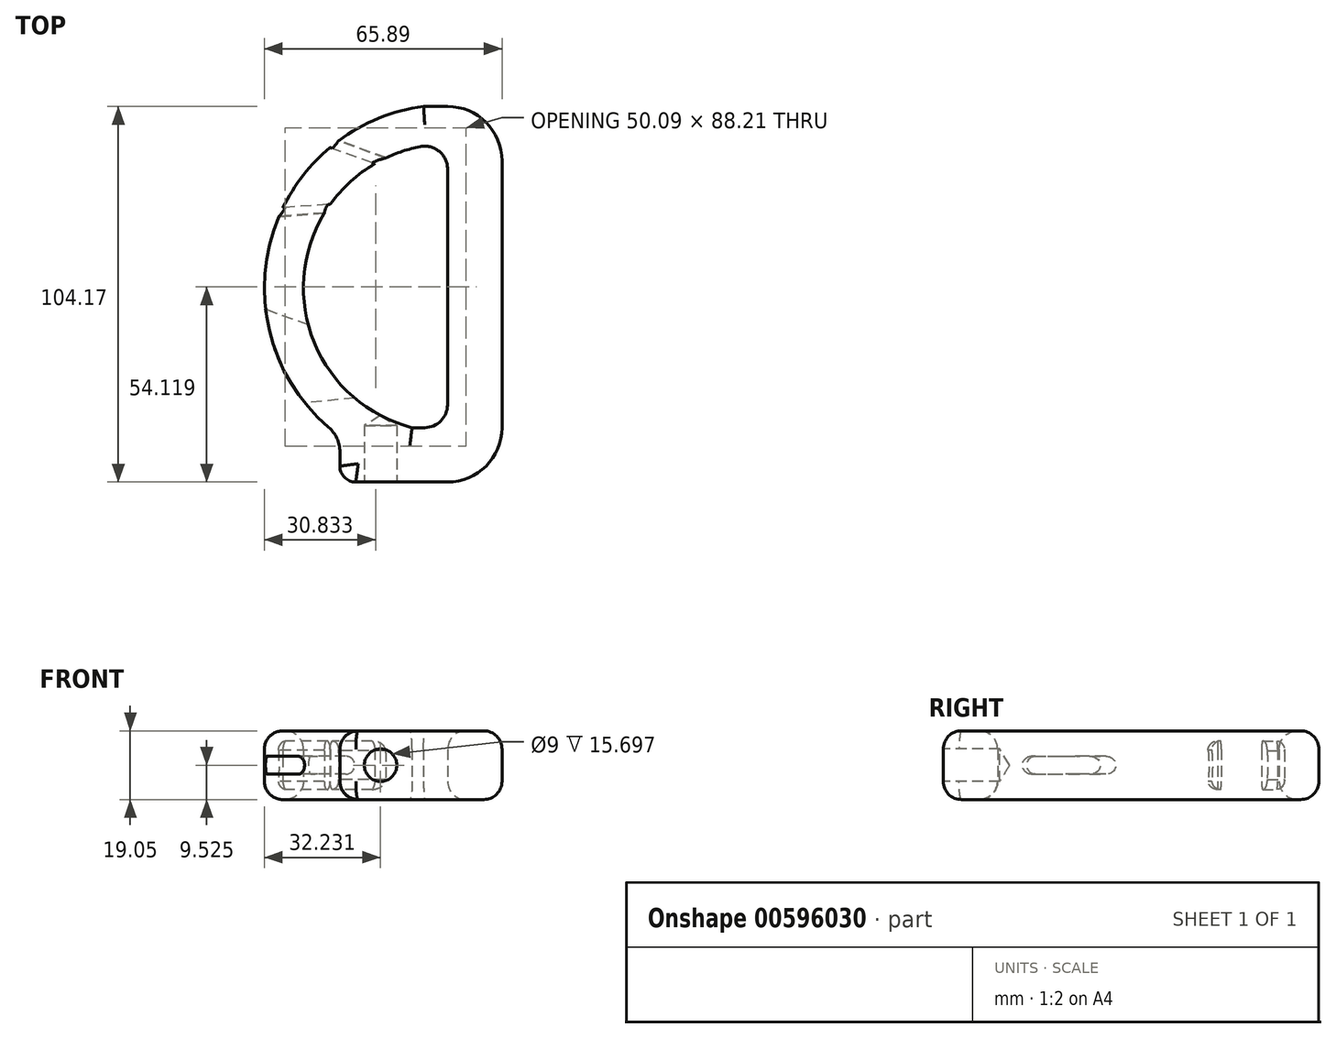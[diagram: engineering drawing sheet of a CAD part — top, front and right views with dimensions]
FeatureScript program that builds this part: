
annotation { "Feature Type Name" : "Feature", "Feature Type Description" : "" }
export const myFeature = defineFeature(function(context is Context, id is Id, definition is map)
    precondition{}
    {
        {
            var Q0;
            Q0=qCreatedBy(makeId("Top.planeOp"),FACE);
            var sketch = newSketch(context, id + "F0", { "sketchPlane" : qUnion([Q0])});
            skArc(sketch, "E0", {"start": v(-6.66, 50.36) * mm, "mid": v(-48.71, 14.41) * mm, "end": v(-33, -38.63) * mm});
            skArc(sketch, "E1", {"start": v(-7.55, 39.23) * mm, "mid": v(-39.93, 1.17) * mm, "end": v(-9.83, -38.72) * mm});
            skLineSegment(sketch, "E2", {"start": v(0, 50.36) * mm, "end": v(-6.66, 50.36) * mm});
            skLineSegment(sketch, "E3", {"start": v(15.1, 35.27) * mm, "end": v(15.1, -38.72) * mm});
            skLineSegment(sketch, "E4", {"start": v(-29.85, -49.4) * mm, "end": v(-29.85, -45.45) * mm});
            skLineSegment(sketch, "E5", {"start": v(0, 33) * mm, "end": v(0, -32.37) * mm});
            skLineSegment(sketch, "E6", {"start": v(-6.35, -38.72) * mm, "end": v(-9.83, -38.72) * mm});
            skPoint(sketch, "E7", {"position": v(-50.8, 0) * mm});
            skPoint(sketch, "E8", {"position": v(-44.25, -24.96) * mm});
            skPoint(sketch, "E9", {"position": v(-47.9, 16.9) * mm});
            skLineSegment(sketch, "E10", {"start": v(-25.43, -53.8) * mm, "end": v(0, -53.8) * mm});
            skPoint(sketch, "E11.visualSharp", {"position": v(15.1, -53.8) * mm});
            skArc(sketch, "E11.filletArc", {"start": v(0, -53.8) * mm, "mid": v(10.67, -49.39) * mm, "end": v(15.1, -38.72) * mm});
            skPoint(sketch, "E12.visualSharp", {"position": v(15.1, 50.36) * mm});
            skArc(sketch, "E12.filletArc", {"start": v(15.1, 35.27) * mm, "mid": v(10.67, 45.94) * mm, "end": v(0, 50.36) * mm});
            skPoint(sketch, "E13.visualSharp", {"position": v(-29.85, -41.1) * mm});
            skArc(sketch, "E13.filletArc", {"start": v(-29.85, -45.45) * mm, "mid": v(-30.67, -41.7) * mm, "end": v(-33, -38.63) * mm});
            skPoint(sketch, "E14.visualSharp", {"position": v(-29.85, -53.8) * mm});
            skArc(sketch, "E14.filletArc", {"start": v(-29.85, -49.4) * mm, "mid": v(-28.55, -52.51) * mm, "end": v(-25.43, -53.8) * mm});
            skPoint(sketch, "E15.visualSharp", {"position": v(0, 39.95) * mm});
            skArc(sketch, "E15.filletArc", {"start": v(0, 33) * mm, "mid": v(-2.3, 37.89) * mm, "end": v(-7.55, 39.23) * mm});
            skArc(sketch, "E16.filletArc", {"start": v(-6.35, -38.72) * mm, "mid": v(-1.86, -36.86) * mm, "end": v(0, -32.37) * mm});
            skPoint(sketch, "E17", {"position": v(-50.65, -3.9) * mm});
            skPoint(sketch, "E18", {"position": v(-36.28, 35.56) * mm});
            skSolve(sketch);
        }
        {
            var Q0;
            Q0=makeQuery(id+"F0.imprint","IMPRINT",FACE,{"disambiguationData":[TD([[makeQuery(id+"F0.imprint","IMPRINT",EDGE,{"derivedFrom":sQuery(id+"F0.wireOp",EDGE,"E0")}),1.0]])]});
            extrude(context, id + "F1", {"entities" : qUnion([Q0]), "depth" : 19.05 * mm, "offsetDistance" : 25.4 * mm});
        }
        {
            var Q0;
            Q0=makeQuery(id+"F1.opExtrude","SWEPT_FACE",FACE,{"disambiguationData":[OSD([sQuery(id+"F0.wireOp",EDGE,"E5")])]});
            cPlane(context, id + "F2", {"entities" : qUnion([Q0]), "cplaneType" : CPlaneType.OFFSET, "offset" : 50.8 * mm, "width" : 152.4 * mm, "height" : 152.4 * mm});
        }
        {
            var Q0;
            Q0=makeQuery(id+"F1.opExtrude","SWEPT_FACE",FACE,{"disambiguationData":[OSD([sQuery(id+"F0.wireOp",EDGE,"E10")])]});
            var sketch = newSketch(context, id + "F3", { "sketchPlane" : qUnion([Q0])});
            skPoint(sketch, "E19", {"position": v(-18.57, 9.53) * mm});
            skSolve(sketch);
        }
        {
            var Q0;
            Q0=sQuery(id+"F3.wireOp",VERTEX,"E19");
            var Q1;
            Q1=makeQuery(id+"F1.opExtrude","SWEPT_BODY",BODY,{"disambiguationData":[OSD([sQuery(id+"F0.wireOp",EDGE,"E0"),sQuery(id+"F0.wireOp",EDGE,"E1"),sQuery(id+"F0.wireOp",EDGE,"E2"),sQuery(id+"F0.wireOp",EDGE,"E3"),sQuery(id+"F0.wireOp",EDGE,"E4"),sQuery(id+"F0.wireOp",EDGE,"E5"),sQuery(id+"F0.wireOp",EDGE,"E6"),sQuery(id+"F0.wireOp",EDGE,"E10")])]});
            hole(context, id + "F4", {"style" : HoleStyle.SIMPLE, "endStyle" : HoleEndStyle.BLIND, "standardTappedOrClearance" : lookupTablePath({ "standard" : "ISO", "engagement" : "75%", "pitch" : "1 mm", "size" : "M10", "type" : "Tapped" }), "standardBlindInLast" : lookupTablePath({ "standard" : "ISO", "engagement" : "75%", "pitch" : "1 mm", "size" : "M10", "type" : "Tapped" }), "holeDiameter" : 9 * mm, "showTappedDepth" : true, "holeDepth" : 15.7 * mm, "isTappedThrough" : true, "tappedDepth" : 12.7 * mm, "tapClearance" : 3, "locations" : qUnion([Q0]), "scope" : qUnion([Q1]), "majorDiameter" : 10 * mm});
        }
        {
            var Q0;
            Q0=qCreatedBy(id+"F2.planeOp",FACE);
            var sketch = newSketch(context, id + "F5", { "sketchPlane" : qUnion([Q0])});
            skPoint(sketch, "E20", {"position": v(-17.21, 0) * mm});
            skPoint(sketch, "E21", {"position": v(-35.87, 0) * mm});
            skPoint(sketch, "E22", {"position": v(3.6, 0) * mm});
            skPoint(sketch, "E23", {"position": v(24.65, 0) * mm});
            skLineSegment(sketch, "E24", {"start": v(-35.87, 0) * mm, "end": v(-35.87, 19.05) * mm});
            skLineSegment(sketch, "E25", {"start": v(-17.21, 0) * mm, "end": v(-17.21, 19.05) * mm});
            skLineSegment(sketch, "E26", {"start": v(3.6, 0) * mm, "end": v(3.6, 7.02) * mm});
            skLineSegment(sketch, "E27", {"start": v(24.65, 0) * mm, "end": v(24.65, 7.02) * mm});
            skArc(sketch, "E28", {"start": v(-35.87, 16.26) * mm, "mid": v(-37.56, 15.6) * mm, "end": v(-38.36, 13.97) * mm});
            skArc(sketch, "E29.MirrorCS", {"start": v(-35.87, 2.8) * mm, "mid": v(-37.56, 3.45) * mm, "end": v(-38.36, 5.08) * mm});
            skArc(sketch, "E30", {"start": v(-38.36, 13.97) * mm, "mid": v(-38.54, 9.52) * mm, "end": v(-38.36, 5.08) * mm});
            skLineSegment(sketch, "E31", {"start": v(-35.87, 5.3) * mm, "end": v(-35.87, 13.76) * mm});
            skPoint(sketch, "E32", {"position": v(-35.87, 9.52) * mm});
            skLineSegment(sketch, "E33", {"start": v(-1.84, -3.07) * mm, "end": v(-1.84, 15.98) * mm});
            skArc(sketch, "E34", {"start": v(-14.72, 13.55) * mm, "mid": v(-15.37, 15.45) * mm, "end": v(-17.21, 16.26) * mm});
            skArc(sketch, "E35.MirrorCS", {"start": v(-14.72, 5.5) * mm, "mid": v(-15.37, 3.6) * mm, "end": v(-17.21, 2.8) * mm});
            skArc(sketch, "E36", {"start": v(-14.72, 13.55) * mm, "mid": v(-14.89, 9.52) * mm, "end": v(-14.72, 5.5) * mm});
            skLineSegment(sketch, "E37", {"start": v(-17.21, 5.3) * mm, "end": v(-17.21, 13.76) * mm});
            skPoint(sketch, "E38", {"position": v(-17.21, 9.53) * mm});
            skLineSegment(sketch, "E39", {"start": v(-35.87, 2.8) * mm, "end": v(-17.21, 2.8) * mm});
            skLineSegment(sketch, "E40", {"start": v(-35.87, 16.26) * mm, "end": v(-17.21, 16.26) * mm});
            skArc(sketch, "E41", {"start": v(3.6, 12.03) * mm, "mid": v(1.1, 9.52) * mm, "end": v(3.6, 7.02) * mm});
            skArc(sketch, "E42", {"start": v(24.65, 7.02) * mm, "mid": v(27.15, 9.52) * mm, "end": v(24.65, 12.03) * mm});
            skLineSegment(sketch, "E43", {"start": v(3.6, 12.03) * mm, "end": v(24.65, 12.03) * mm});
            skLineSegment(sketch, "E44", {"start": v(3.6, 7.02) * mm, "end": v(24.65, 7.02) * mm});
            skLineSegment(sketch, "E45.trimOffspring", {"start": v(3.6, 12.03) * mm, "end": v(3.6, 19.05) * mm});
            skLineSegment(sketch, "E46.trimOffspring", {"start": v(24.65, 12.03) * mm, "end": v(24.65, 19.05) * mm});
            skSolve(sketch);
        }
        {
            var Q0;
            Q0=sQuery(id+"F5.wireOp",EDGE,"E33");
            cPlane(context, id + "F6", {"entities" : qUnion([Q0]), "cplaneType" : CPlaneType.LINE_ANGLE, "offset" : 25.4 * mm, "angle" : 20 * degree, "oppositeDirection" : true, "width" : 152.4 * mm, "height" : 152.4 * mm});
        }
        {
            var Q0;
            Q0=qCreatedBy(id+"F6.planeOp",FACE);
            cPlane(context, id + "F7", {"entities" : qUnion([Q0]), "cplaneType" : CPlaneType.OFFSET, "offset" : 12.7 * mm, "oppositeDirection" : true, "width" : 152.4 * mm, "height" : 152.4 * mm});
        }
        {
            var Q0;
            Q0=qCreatedBy(id+"F7.planeOp",FACE);
            var sketch = newSketch(context, id + "F8", { "sketchPlane" : qUnion([Q0])});
            skPoint(sketch, "E47", {"position": v(25.47, 0) * mm});
            skLineSegment(sketch, "E48", {"start": v(13.01, 2.8) * mm, "end": v(13.01, 16.26) * mm});
            skLineSegment(sketch, "E49", {"start": v(25.47, 0) * mm, "end": v(25.47, 19.05) * mm});
            skLineSegment(sketch, "E50", {"start": v(13.01, 5.3) * mm, "end": v(13.01, 13.76) * mm});
            skPoint(sketch, "E51", {"position": v(13.01, 9.53) * mm});
            skArc(sketch, "E52", {"start": v(27.97, 13.55) * mm, "mid": v(27.31, 15.45) * mm, "end": v(25.47, 16.26) * mm});
            skArc(sketch, "E53.MirrorCS", {"start": v(27.97, 5.5) * mm, "mid": v(27.31, 3.6) * mm, "end": v(25.47, 2.8) * mm});
            skLineSegment(sketch, "E54", {"start": v(25.47, 5.3) * mm, "end": v(25.47, 13.76) * mm});
            skPoint(sketch, "E55", {"position": v(25.47, 9.53) * mm});
            skLineSegment(sketch, "E56", {"start": v(13.01, 2.8) * mm, "end": v(25.47, 2.8) * mm});
            skLineSegment(sketch, "E57", {"start": v(13.01, 16.26) * mm, "end": v(25.47, 16.26) * mm});
            skArc(sketch, "E58", {"start": v(27.97, 5.5) * mm, "mid": v(28.12, 9.53) * mm, "end": v(27.97, 13.55) * mm});
            skSolve(sketch);
        }
        {
            var Q0;
            Q0=sQuery(id+"F5.wireOp",EDGE,"E33");
            cPlane(context, id + "F9", {"entities" : qUnion([Q0]), "cplaneType" : CPlaneType.LINE_ANGLE, "offset" : 25.4 * mm, "angle" : 4.42 * degree, "width" : 152.4 * mm, "height" : 152.4 * mm});
        }
        {
            var Q0;
            Q0=qCreatedBy(id+"F9.planeOp",FACE);
            cPlane(context, id + "F10", {"entities" : qUnion([Q0]), "cplaneType" : CPlaneType.OFFSET, "offset" : 15.24 * mm, "oppositeDirection" : true, "width" : 152.4 * mm, "height" : 152.4 * mm});
        }
        {
            var Q0;
            Q0=qCreatedBy(id+"F10.planeOp",FACE);
            var sketch = newSketch(context, id + "F11", { "sketchPlane" : qUnion([Q0])});
            skPoint(sketch, "E59", {"position": v(33.33, 0) * mm});
            skPoint(sketch, "E60", {"position": v(25.7, 0) * mm});
            skLineSegment(sketch, "E61", {"start": v(25.7, 0) * mm, "end": v(25.7, 19.05) * mm});
            skLineSegment(sketch, "E62", {"start": v(33.33, 0) * mm, "end": v(33.33, 19.05) * mm});
            skArc(sketch, "E63", {"start": v(25.7, 16.26) * mm, "mid": v(23.93, 15.52) * mm, "end": v(23.2, 13.73) * mm});
            skArc(sketch, "E64.MirrorCS", {"start": v(25.7, 2.8) * mm, "mid": v(24.02, 3.45) * mm, "end": v(23.22, 5.08) * mm});
            skLineSegment(sketch, "E65", {"start": v(25.7, 5.3) * mm, "end": v(25.7, 13.76) * mm});
            skPoint(sketch, "E66", {"position": v(25.7, 9.52) * mm});
            skArc(sketch, "E67", {"start": v(35.82, 13.55) * mm, "mid": v(35.17, 15.45) * mm, "end": v(33.33, 16.26) * mm});
            skArc(sketch, "E68.MirrorCS", {"start": v(35.82, 5.5) * mm, "mid": v(35.17, 3.6) * mm, "end": v(33.33, 2.8) * mm});
            skArc(sketch, "E69", {"start": v(35.82, 13.55) * mm, "mid": v(35.65, 9.52) * mm, "end": v(35.82, 5.5) * mm});
            skLineSegment(sketch, "E70", {"start": v(33.33, 5.3) * mm, "end": v(33.33, 13.76) * mm});
            skPoint(sketch, "E71", {"position": v(33.33, 9.52) * mm});
            skLineSegment(sketch, "E72", {"start": v(25.7, 2.8) * mm, "end": v(33.33, 2.8) * mm});
            skLineSegment(sketch, "E73", {"start": v(25.7, 16.26) * mm, "end": v(33.33, 16.26) * mm});
            skArc(sketch, "E74", {"start": v(23.22, 5.08) * mm, "mid": v(23.4, 9.4) * mm, "end": v(23.2, 13.73) * mm});
            skSolve(sketch);
        }
        {
            var Q0;
            {var subQ1=sQuery(id+"F8.wireOp",EDGE,"E52");Q0=makeQuery(id+"F8.imprint","IMPRINT",FACE,{"disambiguationData":[TD([[makeQuery(id+"F8.imprint","IMPRINT",EDGE,{"derivedFrom":subQ1}),1.0]])]});}
            var Q1;
            {var subQ5=sQuery(id+"F8.wireOp",EDGE,"E50");Q1=makeQuery(id+"F8.imprint","IMPRINT",FACE,{"disambiguationData":[TD([[makeQuery(id+"F8.imprint","IMPRINT",EDGE,{"derivedFrom":subQ5}),-1.0]])]});}
            var Q2;
            {var subQ0=sQuery(id+"F8.wireOp",EDGE,"79d6455e-a1dc-483f-a46f-3cff99740c98");Q2=makeQuery(id+"F8.imprint","IMPRINT",FACE,{"disambiguationData":[TD([[makeQuery(id+"F8.imprint","IMPRINT",EDGE,{"derivedFrom":subQ0}),1.0]])]});}
            extrude(context, id + "F12", {"entities" : qUnion([Q0, Q1, Q2]), "operationType" : NewBodyOperationType.REMOVE, "depth" : 38.1 * mm, "offsetDistance" : 25.4 * mm});
        }
        {
            var Q0;
            {var subQ5=sQuery(id+"F11.wireOp",EDGE,"E65");Q0=makeQuery(id+"F11.imprint","IMPRINT",FACE,{"disambiguationData":[TD([[makeQuery(id+"F11.imprint","IMPRINT",EDGE,{"derivedFrom":subQ5}),-1.0]])]});}
            var Q1;
            {var subQ0=sQuery(id+"F11.wireOp",EDGE,"E63");Q1=makeQuery(id+"F11.imprint","IMPRINT",FACE,{"disambiguationData":[TD([[makeQuery(id+"F11.imprint","IMPRINT",EDGE,{"derivedFrom":subQ0}),1.0]])]});}
            extrude(context, id + "F13", {"entities" : qUnion([Q0, Q1]), "operationType" : NewBodyOperationType.REMOVE, "depth" : 44.45 * mm, "offsetDistance" : 25.4 * mm});
        }
        {
            var Q0;
            Q0=sQuery(id+"F5.wireOp",EDGE,"E33");
            cPlane(context, id + "F14", {"entities" : qUnion([Q0]), "cplaneType" : CPlaneType.LINE_ANGLE, "offset" : 25.4 * mm, "angle" : 20 * degree, "oppositeDirection" : true, "width" : 152.4 * mm, "height" : 152.4 * mm});
        }
        {
            var Q0;
            Q0=qCreatedBy(id+"F14.planeOp",FACE);
            var sketch = newSketch(context, id + "F15", { "sketchPlane" : qUnion([Q0])});
            skArc(sketch, "E75", {"start": v(-25.33, 7.02) * mm, "mid": v(-22.83, 9.52) * mm, "end": v(-25.33, 12.03) * mm});
            skLineSegment(sketch, "E76", {"start": v(-35.49, 12.03) * mm, "end": v(-25.33, 12.03) * mm});
            skLineSegment(sketch, "E77", {"start": v(-35.49, 7.02) * mm, "end": v(-25.33, 7.02) * mm});
            skLineSegment(sketch, "E78", {"start": v(-35.49, 7.02) * mm, "end": v(-35.49, 12.03) * mm});
            skSolve(sketch);
        }
        {
            var Q0;
            Q0=sQuery(id+"F5.wireOp",EDGE,"E33");
            cPlane(context, id + "F16", {"entities" : qUnion([Q0]), "cplaneType" : CPlaneType.LINE_ANGLE, "offset" : 25.4 * mm, "angle" : 5 * degree, "width" : 152.4 * mm, "height" : 152.4 * mm});
        }
        {
            var Q0;
            Q0=qCreatedBy(id+"F16.planeOp",FACE);
            cPlane(context, id + "F17", {"entities" : qUnion([Q0]), "cplaneType" : CPlaneType.OFFSET, "offset" : 38.1 * mm, "oppositeDirection" : true, "width" : 152.4 * mm, "height" : 152.4 * mm});
        }
        {
            var Q0;
            Q0=qCreatedBy(id+"F17.planeOp",FACE);
            var sketch = newSketch(context, id + "F18", { "sketchPlane" : qUnion([Q0])});
            skLineSegment(sketch, "E79.bottom", {"start": v(-12.62, 7.03) * mm, "end": v(-25.7, 7.03) * mm});
            skLineSegment(sketch, "E79.top", {"start": v(-12.62, 12.03) * mm, "end": v(-25.7, 12.03) * mm});
            skArc(sketch, "E80", {"start": v(-25.7, 12.03) * mm, "mid": v(-28.2, 9.53) * mm, "end": v(-25.7, 7.03) * mm});
            skLineSegment(sketch, "E81", {"start": v(-12.62, 12.03) * mm, "end": v(-12.62, 7.03) * mm});
            skSolve(sketch);
        }
        {
            var Q0;
            Q0=makeQuery(id+"F18.imprint","IMPRINT",FACE,{"disambiguationData":[TD([[makeQuery(id+"F18.imprint","IMPRINT",EDGE,{"derivedFrom":sQuery(id+"F18.wireOp",EDGE,"E79.bottom")}),-1.0]])]});
            var Q1;
            Q1=makeQuery(id+"F1.opExtrude","SWEPT_FACE",FACE,{"disambiguationData":[OSD([sQuery(id+"F0.wireOp",EDGE,"E5")])]});
            extrude(context, id + "F19", {"entities" : qUnion([Q0]), "operationType" : NewBodyOperationType.REMOVE, "depth" : 76.2 * mm, "endBoundEntityFace" : qUnion([Q1]), "offsetDistance" : 25.4 * mm});
        }
        {
            var Q0;
            Q0=qSketchRegion(id+"F15",true);
            extrude(context, id + "F20", {"entities" : qUnion([Q0]), "operationType" : NewBodyOperationType.REMOVE, "depth" : 20.32 * mm, "offsetDistance" : 25.4 * mm});
        }
        {
            var Q0;
            Q0=makeQuery(id+"F1.opExtrude","CAP_EDGE",EDGE,{"disambiguationData":[OSD([sQuery(id+"F0.wireOp",EDGE,"E5")])],"isStart":true});
            var Q1;
            Q1=makeQuery(id+"F1.opExtrude","CAP_EDGE",EDGE,{"disambiguationData":[OSD([sQuery(id+"F0.wireOp",EDGE,"E5")])],"isStart":false});
            var Q2;
            Q2=makeQuery(id+"F1.opExtrude","CAP_EDGE",EDGE,{"disambiguationData":[OSD([sQuery(id+"F0.wireOp",EDGE,"E3")])],"isStart":false});
            var Q3;
            Q3=makeQuery(id+"F1.opExtrude","CAP_EDGE",EDGE,{"disambiguationData":[OSD([sQuery(id+"F0.wireOp",EDGE,"E0")])],"isStart":true});
            fillet(context, id + "F21", {"entities" : qUnion([Q0, Q1, Q2, Q3]), "radius" : 5.08 * mm, "tangentPropagation" : true, "allowEdgeOverflow" : false});
        }
    });
